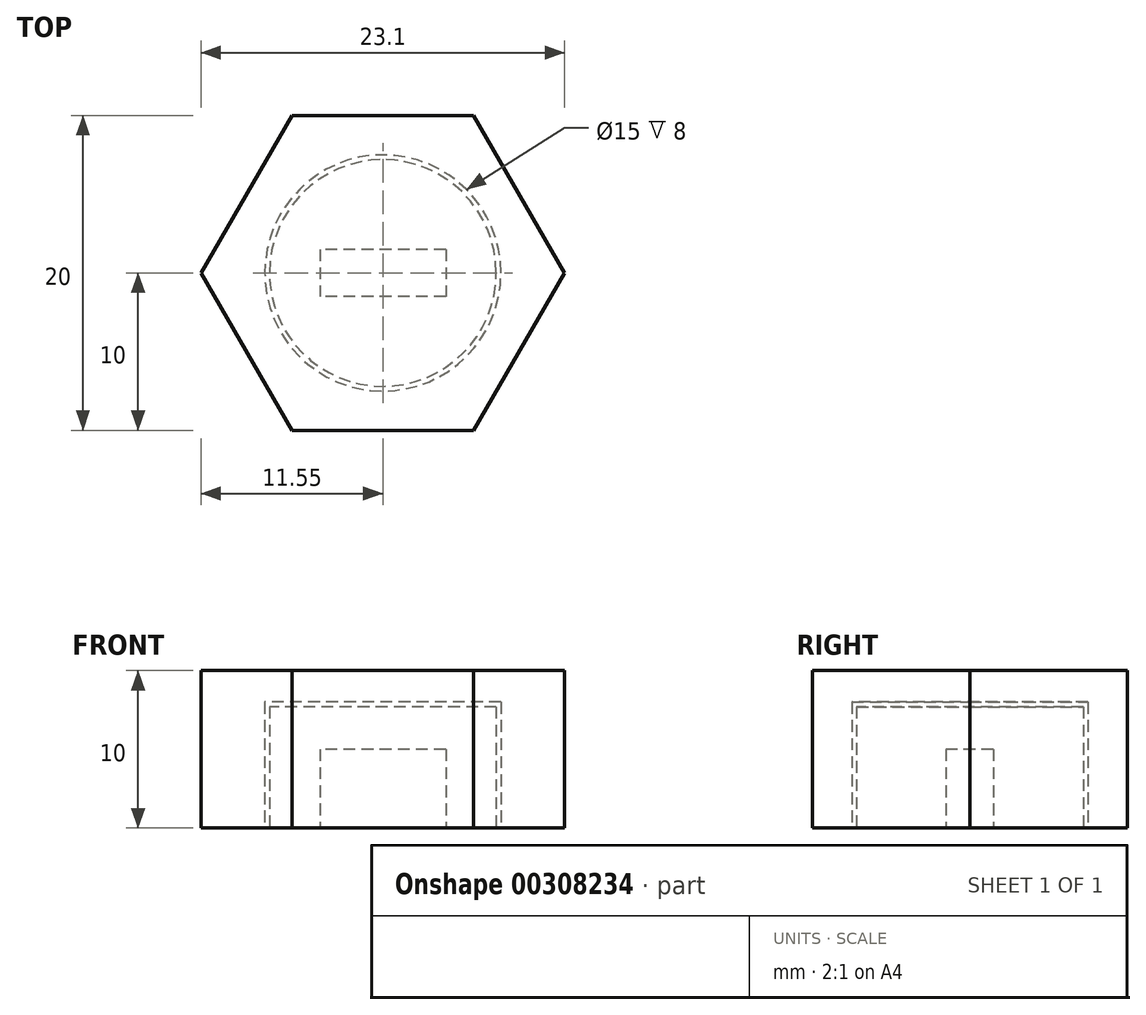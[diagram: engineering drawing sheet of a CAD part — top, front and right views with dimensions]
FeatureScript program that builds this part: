
annotation { "Feature Type Name" : "Feature", "Feature Type Description" : "" }
export const myFeature = defineFeature(function(context is Context, id is Id, definition is map)
    precondition{}
    {
        {
            assignVariable(context, id + "F0", {"name" : "gap_vert", "anyValue" : 0.3});
        }
        {
            var Q0;
            Q0=qCreatedBy(makeId("Top.planeOp"),FACE);
            var sketch = newSketch(context, id + "F1", { "sketchPlane" : qUnion([Q0])});
            skCircle(sketch, "E0", {"center": v(0, 0) * mm, "radius": 10 * mm});
            skCircle(sketch, "E1", {"center": v(0, 0) * mm, "radius": 7.5 * mm});
            skCircle(sketch, "E2", {"center": v(0, 0) * mm, "radius": 7.2 * mm});
            skLineSegment(sketch, "E3.bottom", {"start": v(4, 1.5) * mm, "end": v(-4, 1.5) * mm});
            skLineSegment(sketch, "E3.top", {"start": v(4, -1.5) * mm, "end": v(-4, -1.5) * mm});
            skLineSegment(sketch, "E3.left", {"start": v(4, 1.5) * mm, "end": v(4, -1.5) * mm});
            skLineSegment(sketch, "E3.right", {"start": v(-4, 1.5) * mm, "end": v(-4, -1.5) * mm});
            skCircle(sketch, "E4.cCircle", {"center": v(0, 0) * mm, "radius": 10 * mm, "construction": true});
            skLineSegment(sketch, "E4.0", {"start": v(-5.77, 10) * mm, "end": v(5.77, 10) * mm});
            skLineSegment(sketch, "E4.1", {"start": v(5.77, 10) * mm, "end": v(11.55, 0) * mm});
            skLineSegment(sketch, "E4.2", {"start": v(11.55, 0) * mm, "end": v(5.77, -10) * mm});
            skLineSegment(sketch, "E4.3", {"start": v(5.77, -10) * mm, "end": v(-5.77, -10) * mm});
            skLineSegment(sketch, "E4.4", {"start": v(-5.77, -10) * mm, "end": v(-11.55, 0) * mm});
            skLineSegment(sketch, "E4.5", {"start": v(-11.55, 0) * mm, "end": v(-5.77, 10) * mm});
            skPoint(sketch, "E4.0.midPoint", {"position": v(0, 10) * mm});
            skSolve(sketch);
        }
        {
            var Q0;
            Q0=makeQuery(id+"F1.imprint","IMPRINT",FACE,{"disambiguationData":[TD([[makeQuery(id+"F1.imprint","IMPRINT",EDGE,{"derivedFrom":sQuery(id+"F1.wireOp",EDGE,"E0")}),1.0]])]});
            var Q1;
            Q1=makeQuery(id+"F1.imprint","IMPRINT",FACE,{"disambiguationData":[TD([[makeQuery(id+"F1.imprint","IMPRINT",EDGE,{"derivedFrom":sQuery(id+"F1.wireOp",EDGE,"E1")}),1.0]])]});
            var Q2;
            Q2=makeQuery(id+"F1.imprint","IMPRINT",FACE,{"disambiguationData":[TD([[makeQuery(id+"F1.imprint","IMPRINT",EDGE,{"derivedFrom":sQuery(id+"F1.wireOp",EDGE,"E2")}),1.0]])]});
            var Q3;
            Q3=makeQuery(id+"F1.imprint","IMPRINT",FACE,{"disambiguationData":[TD([[makeQuery(id+"F1.imprint","IMPRINT",EDGE,{"derivedFrom":sQuery(id+"F1.wireOp",EDGE,"E3.bottom")}),1.0]])]});
            var Q4;
            {var subQ0=sQuery(id+"F1.wireOp",EDGE,"E4.0");var subQ1=sQuery(id+"F1.wireOp",EDGE,"E0");var subQ2=makeQuery(id+"F1.imprint","INTERSECT",VERTEX,{"derivedFrom":[subQ1,subQ0]});Q4=makeQuery(id+"F1.imprint","IMPRINT",FACE,{"disambiguationData":[TD([[makeQuery(id+"F1.imprint","IMPRINT",EDGE,{"disambiguationData":[TD([[subQ2,-1.0]])],"derivedFrom":subQ1}),-1.0]])]});}
            var Q5;
            {var subQ0=sQuery(id+"F1.wireOp",EDGE,"E4.0");var subQ1=sQuery(id+"F1.wireOp",EDGE,"E0");var subQ2=makeQuery(id+"F1.imprint","INTERSECT",VERTEX,{"derivedFrom":[subQ1,subQ0]});Q5=makeQuery(id+"F1.imprint","IMPRINT",FACE,{"disambiguationData":[TD([[makeQuery(id+"F1.imprint","IMPRINT",EDGE,{"disambiguationData":[TD([[subQ2,1.0]])],"derivedFrom":subQ1}),-1.0]])]});}
            var Q6;
            {var subQ0=sQuery(id+"F1.wireOp",EDGE,"E4.1");var subQ1=sQuery(id+"F1.wireOp",EDGE,"E0");var subQ2=makeQuery(id+"F1.imprint","INTERSECT",VERTEX,{"derivedFrom":[subQ1,subQ0]});Q6=makeQuery(id+"F1.imprint","IMPRINT",FACE,{"disambiguationData":[TD([[makeQuery(id+"F1.imprint","IMPRINT",EDGE,{"disambiguationData":[TD([[subQ2,1.0]])],"derivedFrom":subQ1}),-1.0]])]});}
            var Q7;
            {var subQ0=sQuery(id+"F1.wireOp",EDGE,"E4.3");var subQ1=sQuery(id+"F1.wireOp",EDGE,"E0");var subQ2=makeQuery(id+"F1.imprint","INTERSECT",VERTEX,{"derivedFrom":[subQ1,subQ0]});Q7=makeQuery(id+"F1.imprint","IMPRINT",FACE,{"disambiguationData":[TD([[makeQuery(id+"F1.imprint","IMPRINT",EDGE,{"disambiguationData":[TD([[subQ2,-1.0]])],"derivedFrom":subQ1}),-1.0]])]});}
            var Q8;
            {var subQ0=sQuery(id+"F1.wireOp",EDGE,"E4.4");var subQ1=sQuery(id+"F1.wireOp",EDGE,"E0");var subQ2=makeQuery(id+"F1.imprint","INTERSECT",VERTEX,{"derivedFrom":[subQ1,subQ0]});Q8=makeQuery(id+"F1.imprint","IMPRINT",FACE,{"disambiguationData":[TD([[makeQuery(id+"F1.imprint","IMPRINT",EDGE,{"disambiguationData":[TD([[subQ2,-1.0]])],"derivedFrom":subQ1}),-1.0]])]});}
            var Q9;
            {var subQ0=sQuery(id+"F1.wireOp",EDGE,"E4.5");var subQ1=sQuery(id+"F1.wireOp",EDGE,"E0");var subQ2=makeQuery(id+"F1.imprint","INTERSECT",VERTEX,{"derivedFrom":[subQ1,subQ0]});Q9=makeQuery(id+"F1.imprint","IMPRINT",FACE,{"disambiguationData":[TD([[makeQuery(id+"F1.imprint","IMPRINT",EDGE,{"disambiguationData":[TD([[subQ2,-1.0]])],"derivedFrom":subQ1}),-1.0]])]});}
            extrude(context, id + "F2", {"entities" : qUnion([Q0, Q1, Q2, Q3, Q4, Q5, Q6, Q7, Q8, Q9]), "depth" : 10 * mm, "offsetDistance" : 25 * mm});
        }
        {
            var Q0;
            Q0=makeQuery(id+"F1.imprint","IMPRINT",FACE,{"disambiguationData":[TD([[makeQuery(id+"F1.imprint","IMPRINT",EDGE,{"derivedFrom":sQuery(id+"F1.wireOp",EDGE,"E1")}),1.0]])]});
            var Q1;
            Q1=makeQuery(id+"F1.imprint","IMPRINT",FACE,{"disambiguationData":[TD([[makeQuery(id+"F1.imprint","IMPRINT",EDGE,{"derivedFrom":sQuery(id+"F1.wireOp",EDGE,"E2")}),1.0]])]});
            var Q2;
            Q2=makeQuery(id+"F1.imprint","IMPRINT",FACE,{"disambiguationData":[TD([[makeQuery(id+"F1.imprint","IMPRINT",EDGE,{"derivedFrom":sQuery(id+"F1.wireOp",EDGE,"E3.bottom")}),1.0]])]});
            extrude(context, id + "F3", {"entities" : qUnion([Q0, Q1, Q2]), "operationType" : NewBodyOperationType.REMOVE, "depth" : 8 * mm, "offsetDistance" : 25 * mm});
        }
        {
            var Q0;
            Q0=makeQuery(id+"F1.imprint","IMPRINT",FACE,{"disambiguationData":[TD([[makeQuery(id+"F1.imprint","IMPRINT",EDGE,{"derivedFrom":sQuery(id+"F1.wireOp",EDGE,"E2")}),1.0]])]});
            var Q1;
            Q1=makeQuery(id+"F1.imprint","IMPRINT",FACE,{"disambiguationData":[TD([[makeQuery(id+"F1.imprint","IMPRINT",EDGE,{"derivedFrom":sQuery(id+"F1.wireOp",EDGE,"E3.bottom")}),1.0]])]});
            extrude(context, id + "F4", {"entities" : qUnion([Q0, Q1]), "depth" : (8 - getVariable(context, 'gap_vert')) * mm, "offsetDistance" : 25 * mm});
        }
        {
            var Q0;
            Q0=makeQuery(id+"F1.imprint","IMPRINT",FACE,{"disambiguationData":[TD([[makeQuery(id+"F1.imprint","IMPRINT",EDGE,{"derivedFrom":sQuery(id+"F1.wireOp",EDGE,"E3.bottom")}),1.0]])]});
            extrude(context, id + "F5", {"entities" : qUnion([Q0]), "operationType" : NewBodyOperationType.REMOVE, "depth" : 5 * mm, "offsetDistance" : 25 * mm});
        }
    });
